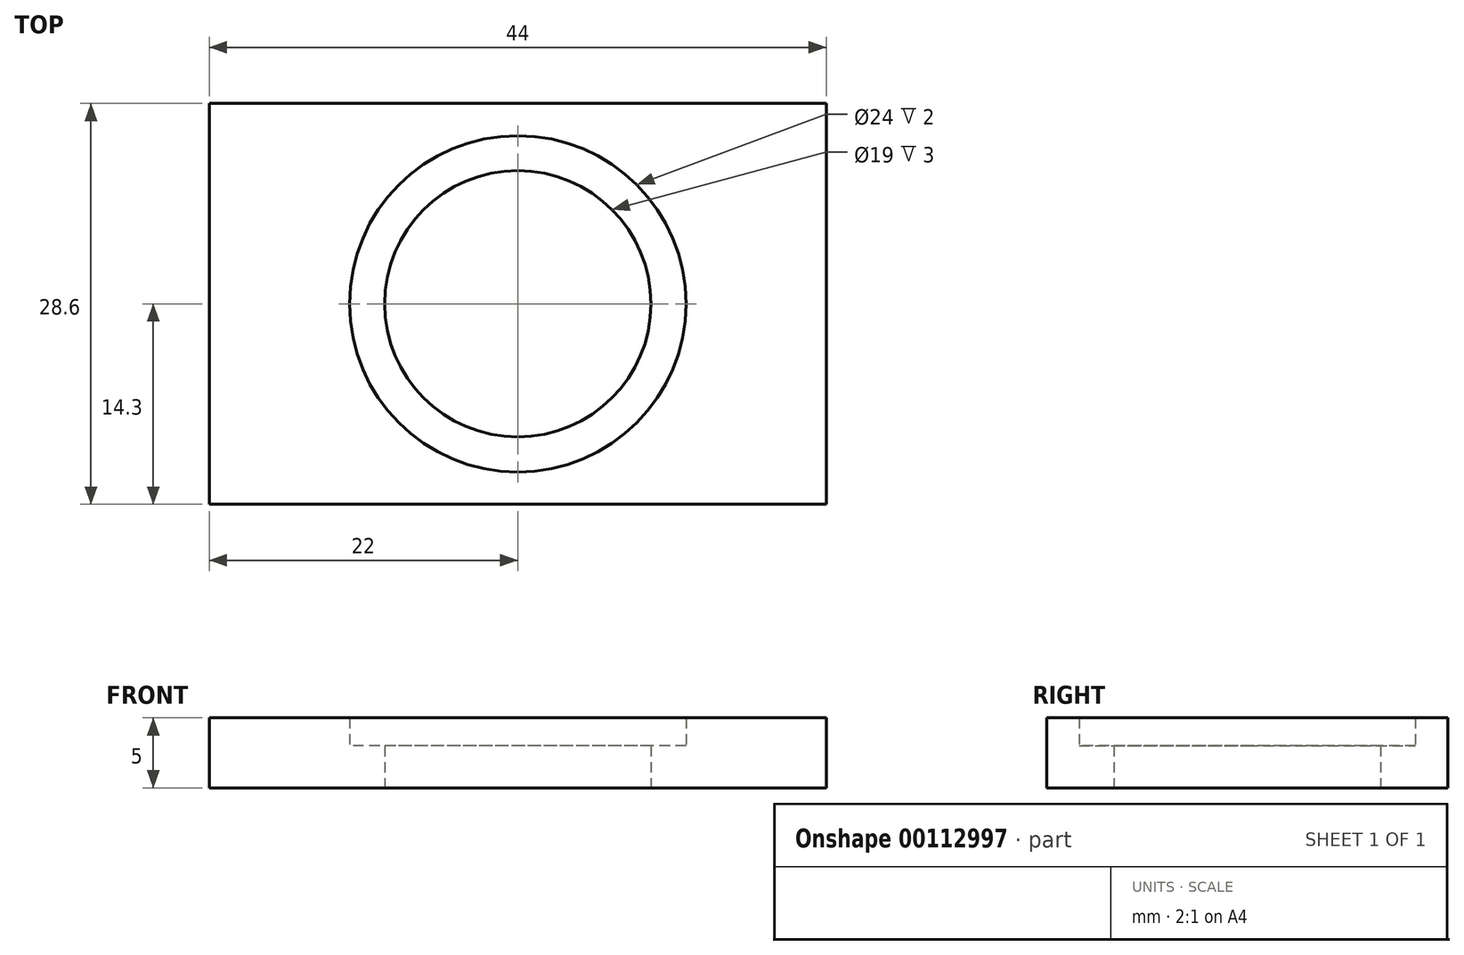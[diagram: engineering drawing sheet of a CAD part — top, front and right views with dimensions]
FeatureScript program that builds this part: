
annotation { "Feature Type Name" : "Feature", "Feature Type Description" : "" }
export const myFeature = defineFeature(function(context is Context, id is Id, definition is map)
    precondition{}
    {
        {
            var Q0;
            Q0=qCreatedBy(makeId("Top.planeOp"),FACE);
            var sketch = newSketch(context, id + "F0", { "sketchPlane" : qUnion([Q0])});
            skLineSegment(sketch, "E0.bottom", {"start": v(0, 0) * mm, "end": v(44, 0) * mm});
            skLineSegment(sketch, "E0.top", {"start": v(0, 28.6) * mm, "end": v(44, 28.6) * mm});
            skLineSegment(sketch, "E0.left", {"start": v(0, 0) * mm, "end": v(0, 28.6) * mm});
            skLineSegment(sketch, "E0.right", {"start": v(44, 0) * mm, "end": v(44, 28.6) * mm});
            skLineSegment(sketch, "E1", {"start": v(22, 28.6) * mm, "end": v(22, 0) * mm, "construction": true});
            skLineSegment(sketch, "E2", {"start": v(0, 14.3) * mm, "end": v(44, 14.3) * mm, "construction": true});
            skCircle(sketch, "E3", {"center": v(22, 14.3) * mm, "radius": 12 * mm});
            skCircle(sketch, "E4", {"center": v(22, 14.3) * mm, "radius": 9.5 * mm});
            skSolve(sketch);
        }
        {
            var Q0;
            Q0=makeQuery(id+"F0.imprint","IMPRINT",FACE,{"disambiguationData":[TD([[makeQuery(id+"F0.imprint","IMPRINT",EDGE,{"derivedFrom":sQuery(id+"F0.wireOp",EDGE,"E0.bottom")}),1.0]])]});
            extrude(context, id + "F1", {"entities" : qUnion([Q0]), "depth" : 5 * mm});
        }
        {
            var Q0;
            Q0=makeQuery(id+"F0.imprint","IMPRINT",FACE,{"disambiguationData":[TD([[makeQuery(id+"F0.imprint","IMPRINT",EDGE,{"derivedFrom":sQuery(id+"F0.wireOp",EDGE,"E3")}),1.0]])]});
            extrude(context, id + "F2", {"entities" : qUnion([Q0]), "operationType" : NewBodyOperationType.ADD, "depth" : 3 * mm});
        }
    });
